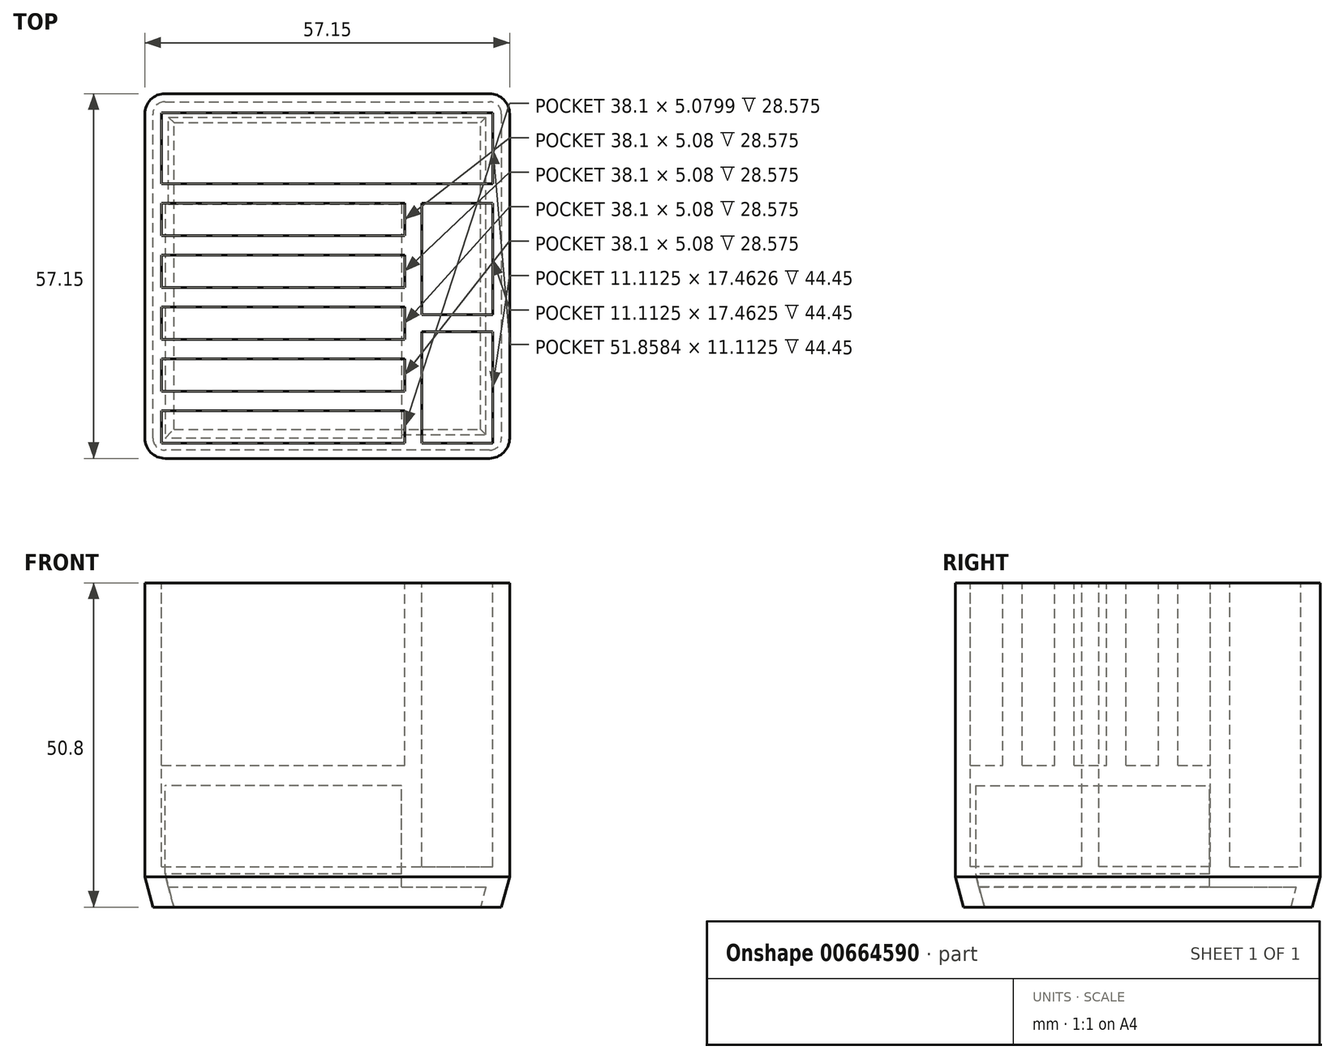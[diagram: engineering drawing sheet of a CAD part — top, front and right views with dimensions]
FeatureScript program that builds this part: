
annotation { "Feature Type Name" : "Feature", "Feature Type Description" : "" }
export const myFeature = defineFeature(function(context is Context, id is Id, definition is map)
    precondition{}
    {
        {
            var Q0;
            Q0=qCreatedBy(makeId("Top.planeOp"),FACE);
            var sketch = newSketch(context, id + "F0", { "sketchPlane" : qUnion([Q0])});
            skLineSegment(sketch, "E0.bottom", {"start": v(0, 0) * mm, "end": v(57.15, 0) * mm});
            skLineSegment(sketch, "E0.top", {"start": v(0, 57.15) * mm, "end": v(57.15, 57.15) * mm});
            skLineSegment(sketch, "E0.left", {"start": v(0, 0) * mm, "end": v(0, 57.15) * mm});
            skLineSegment(sketch, "E0.right", {"start": v(57.15, 0) * mm, "end": v(57.15, 57.15) * mm});
            skSolve(sketch);
        }
        {
            var Q0;
            Q0 = qSketchRegion(id + "F0", true);
            extrude(context, id + "F1", {"entities" : qUnion([Q0]), "depth" : 50.8 * mm - 1 / 203.2 * mm, "offsetDistance" : 25.4 * mm});
        }
        {
            var Q0;
            Q0=makeQuery(id+"F1.opExtrude","CAP_FACE",FACE,{"disambiguationData":[OSD([sQuery(id+"F0.wireOp",EDGE,"E0.bottom"),sQuery(id+"F0.wireOp",EDGE,"E0.top"),sQuery(id+"F0.wireOp",EDGE,"E0.left"),sQuery(id+"F0.wireOp",EDGE,"E0.right")])],"isStart":false});
            var sketch = newSketch(context, id + "F2", { "sketchPlane" : qUnion([Q0])});
            skLineSegment(sketch, "E1.bottom", {"start": v(2.65, 2.38) * mm, "end": v(40.75, 2.38) * mm});
            skLineSegment(sketch, "E1.top", {"start": v(2.65, 7.46) * mm, "end": v(40.75, 7.46) * mm});
            skLineSegment(sketch, "E1.left", {"start": v(2.65, 2.38) * mm, "end": v(2.65, 7.46) * mm});
            skLineSegment(sketch, "E1.right", {"start": v(40.75, 2.38) * mm, "end": v(40.75, 7.46) * mm});
            skLineSegment(sketch, "E2.bottom", {"start": v(43.4, 2.38) * mm, "end": v(54.5, 2.38) * mm});
            skLineSegment(sketch, "E2.top", {"start": v(43.4, 19.84) * mm, "end": v(54.5, 19.84) * mm});
            skLineSegment(sketch, "E2.left", {"start": v(43.4, 2.38) * mm, "end": v(43.4, 19.84) * mm});
            skLineSegment(sketch, "E2.right", {"start": v(54.5, 2.38) * mm, "end": v(54.5, 19.84) * mm});
            skLineSegment(sketch, "E3", {"start": v(2.65, 2.38) * mm, "end": v(0, 2.38) * mm, "construction": true});
            skLineSegment(sketch, "E4", {"start": v(40.75, 2.38) * mm, "end": v(43.4, 2.38) * mm, "construction": true});
            skLineSegment(sketch, "E5", {"start": v(54.5, 2.38) * mm, "end": v(57.15, 2.38) * mm, "construction": true});
            skLineSegment(sketch, "E6.0.1.0", {"start": v(43.4, 39.95) * mm, "end": v(54.5, 39.95) * mm});
            skLineSegment(sketch, "E6.0.1.1", {"start": v(43.4, 22.49) * mm, "end": v(54.5, 22.49) * mm});
            skLineSegment(sketch, "E6.0.1.2", {"start": v(43.4, 22.49) * mm, "end": v(43.4, 39.95) * mm});
            skLineSegment(sketch, "E6.0.1.3", {"start": v(54.5, 22.49) * mm, "end": v(54.5, 39.95) * mm});
            skLineSegment(sketch, "E6.direction1", {"start": v(43.4, 2.38) * mm, "end": v(68.8, 2.38) * mm, "construction": true});
            skLineSegment(sketch, "E7", {"start": v(54.5, 22.49) * mm, "end": v(54.5, 19.84) * mm, "construction": true});
            skLineSegment(sketch, "E8.0.1.0", {"start": v(2.65, 15.58) * mm, "end": v(40.75, 15.58) * mm});
            skLineSegment(sketch, "E8.0.1.1", {"start": v(2.65, 10.5) * mm, "end": v(2.65, 15.58) * mm});
            skLineSegment(sketch, "E8.0.1.2", {"start": v(2.65, 10.5) * mm, "end": v(40.75, 10.5) * mm});
            skLineSegment(sketch, "E8.0.1.3", {"start": v(40.75, 10.5) * mm, "end": v(40.75, 15.58) * mm});
            skLineSegment(sketch, "E8.0.2.0", {"start": v(2.65, 23.7) * mm, "end": v(40.75, 23.7) * mm});
            skLineSegment(sketch, "E8.0.2.1", {"start": v(2.65, 18.63) * mm, "end": v(2.65, 23.7) * mm});
            skLineSegment(sketch, "E8.0.2.2", {"start": v(2.65, 18.63) * mm, "end": v(40.75, 18.63) * mm});
            skLineSegment(sketch, "E8.0.2.3", {"start": v(40.75, 18.63) * mm, "end": v(40.75, 23.7) * mm});
            skLineSegment(sketch, "E8.0.3.0", {"start": v(2.65, 31.83) * mm, "end": v(40.75, 31.83) * mm});
            skLineSegment(sketch, "E8.0.3.1", {"start": v(2.65, 26.75) * mm, "end": v(2.65, 31.83) * mm});
            skLineSegment(sketch, "E8.0.3.2", {"start": v(2.65, 26.75) * mm, "end": v(40.75, 26.75) * mm});
            skLineSegment(sketch, "E8.0.3.3", {"start": v(40.75, 26.75) * mm, "end": v(40.75, 31.83) * mm});
            skLineSegment(sketch, "E8.0.4.0", {"start": v(2.65, 39.95) * mm, "end": v(40.75, 39.95) * mm});
            skLineSegment(sketch, "E8.0.4.1", {"start": v(2.65, 34.87) * mm, "end": v(2.65, 39.95) * mm});
            skLineSegment(sketch, "E8.0.4.2", {"start": v(2.65, 34.87) * mm, "end": v(40.75, 34.87) * mm});
            skLineSegment(sketch, "E8.0.4.3", {"start": v(40.75, 34.87) * mm, "end": v(40.75, 39.95) * mm});
            skLineSegment(sketch, "E9", {"start": v(2.65, 7.46) * mm, "end": v(2.65, 10.5) * mm, "construction": true});
            skLineSegment(sketch, "E10", {"start": v(2.65, 15.58) * mm, "end": v(2.65, 18.63) * mm, "construction": true});
            skLineSegment(sketch, "E11", {"start": v(2.65, 23.7) * mm, "end": v(2.65, 26.75) * mm, "construction": true});
            skLineSegment(sketch, "E12", {"start": v(2.65, 31.83) * mm, "end": v(2.65, 34.87) * mm, "construction": true});
            skLineSegment(sketch, "E13.0.1.0", {"start": v(2.65, 54.1) * mm, "end": v(54.5, 54.1) * mm});
            skLineSegment(sketch, "E13.0.1.1", {"start": v(2.65, 43) * mm, "end": v(54.5, 43) * mm});
            skLineSegment(sketch, "E13.0.1.2", {"start": v(2.65, 43) * mm, "end": v(2.65, 54.1) * mm});
            skLineSegment(sketch, "E13.0.1.3", {"start": v(54.5, 43) * mm, "end": v(54.5, 54.1) * mm});
            skLineSegment(sketch, "E14", {"start": v(2.65, 54.1) * mm, "end": v(2.65, 57.15) * mm, "construction": true});
            skLineSegment(sketch, "E15", {"start": v(2.65, 43) * mm, "end": v(2.65, 39.95) * mm, "construction": true});
            skSolve(sketch);
        }
        {
            var Q0;
            Q0 = qSketchRegion(id + "F2", true);
            extrude(context, id + "F3", {"entities" : qUnion([Q0]), "operationType" : NewBodyOperationType.REMOVE, "oppositeDirection" : true, "depth" : 28.57 * mm, "offsetDistance" : 25.4 * mm});
        }
        {
            var Q0;
            Q0=makeQuery(id+"F3.boolean.opBoolean","COPY",FACE,{"derivedFrom":makeQuery(id+"F3.opExtrude","CAP_FACE",FACE,{"disambiguationData":[OSD([sQuery(id+"F2.wireOp",EDGE,"E13.0.1.0"),sQuery(id+"F2.wireOp",EDGE,"E13.0.1.1"),sQuery(id+"F2.wireOp",EDGE,"E13.0.1.2"),sQuery(id+"F2.wireOp",EDGE,"E13.0.1.3")])],"isStart":false})});
            var sketch = newSketch(context, id + "F4", { "sketchPlane" : qUnion([Q0])});
            skLineSegment(sketch, "E16.1.0", {"start": v(43.4, 39.95) * mm, "end": v(43.4, 22.49) * mm});
            skLineSegment(sketch, "E16.1.1", {"start": v(43.4, 22.49) * mm, "end": v(54.5, 22.49) * mm});
            skLineSegment(sketch, "E16.1.2", {"start": v(54.5, 22.49) * mm, "end": v(54.5, 39.95) * mm});
            skLineSegment(sketch, "E16.1.3", {"start": v(54.5, 39.95) * mm, "end": v(43.4, 39.95) * mm});
            skLineSegment(sketch, "E16.2.0", {"start": v(54.5, 19.84) * mm, "end": v(43.4, 19.84) * mm});
            skLineSegment(sketch, "E16.2.1", {"start": v(43.4, 19.84) * mm, "end": v(43.4, 2.38) * mm});
            skLineSegment(sketch, "E16.2.2", {"start": v(43.4, 2.38) * mm, "end": v(54.5, 2.38) * mm});
            skLineSegment(sketch, "E16.2.3", {"start": v(54.5, 2.38) * mm, "end": v(54.5, 19.84) * mm});
            skLineSegment(sketch, "E17.0", {"start": v(2.65, 54.1) * mm, "end": v(54.5, 54.1) * mm});
            skLineSegment(sketch, "E17.1", {"start": v(54.5, 43) * mm, "end": v(54.5, 54.1) * mm});
            skLineSegment(sketch, "E18.0", {"start": v(2.65, 43) * mm, "end": v(54.5, 43) * mm});
            skLineSegment(sketch, "E18.1", {"start": v(2.65, 43) * mm, "end": v(2.65, 54.1) * mm});
            skSolve(sketch);
        }
        {
            var Q0;
            Q0 = qSketchRegion(id + "F4", true);
            extrude(context, id + "F5", {"entities" : qUnion([Q0]), "operationType" : NewBodyOperationType.REMOVE, "oppositeDirection" : true, "depth" : 19.05 * mm - 3.17 * mm, "offsetDistance" : 25.4 * mm});
        }
        {
            var Q0;
            Q0=makeQuery(id+"F1.opExtrude","SWEPT_EDGE",EDGE,{"disambiguationData":[OSD([sQuery(id+"F0.wireOp",EDGE,"E0.bottom"),sQuery(id+"F0.wireOp",EDGE,"E0.left")])]});
            var Q1;
            Q1=makeQuery(id+"F1.opExtrude","SWEPT_EDGE",EDGE,{"disambiguationData":[OSD([sQuery(id+"F0.wireOp",EDGE,"E0.bottom"),sQuery(id+"F0.wireOp",EDGE,"E0.right")])]});
            var Q2;
            Q2=makeQuery(id+"F1.opExtrude","SWEPT_EDGE",EDGE,{"disambiguationData":[OSD([sQuery(id+"F0.wireOp",EDGE,"E0.top"),sQuery(id+"F0.wireOp",EDGE,"E0.right")])]});
            var Q3;
            Q3=makeQuery(id+"F1.opExtrude","SWEPT_EDGE",EDGE,{"disambiguationData":[OSD([sQuery(id+"F0.wireOp",EDGE,"E0.top"),sQuery(id+"F0.wireOp",EDGE,"E0.left")])]});
            fillet(context, id + "F6", {"entities" : qUnion([Q0, Q1, Q2, Q3]), "radius" : 3.17 * mm, "tangentPropagation" : true, "allowEdgeOverflow" : false});
        }
        {
            var Q0;
            Q0=makeQuery(id+"F1.opExtrude","CAP_EDGE",EDGE,{"disambiguationData":[OSD([sQuery(id+"F0.wireOp",EDGE,"E0.top")])],"isStart":true});
            chamfer(context, id + "F7", {"entities" : qUnion([Q0]), "chamferType" : ChamferType.OFFSET_ANGLE, "width" : 4.76 * mm, "oppositeDirection" : true, "angle" : 15 * degree, "tangentPropagation" : true});
        }
        {
            var Q0;
            Q0=makeQuery(id+"F1.opExtrude","CAP_FACE",FACE,{"disambiguationData":[OSD([sQuery(id+"F0.wireOp",EDGE,"E0.bottom"),sQuery(id+"F0.wireOp",EDGE,"E0.top"),sQuery(id+"F0.wireOp",EDGE,"E0.left"),sQuery(id+"F0.wireOp",EDGE,"E0.right")])],"isStart":true});
            shell(context, id + "F8", {"entities" : qUnion([Q0]), "thickness" : 3.17 * mm});
        }
    });
